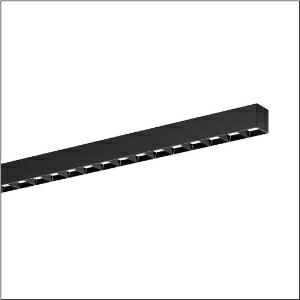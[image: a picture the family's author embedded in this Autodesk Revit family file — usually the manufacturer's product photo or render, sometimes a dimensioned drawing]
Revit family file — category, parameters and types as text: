
# Revit family: silica_r__21_51mx21dc3abb_8748
name_source: partatom
category: Lighting Fixtures
units: mm (PartAtom-declared; Revit-internal decimal feet)

## family parameters
Cut with Voids When Loaded = No
Host = Face
Light Source = No
Part Type = Normal
Room Calculation Point = No
Round Connector Dimension = Use Diameter
Shared = No

## types (1)
- --- (1 x LED, 10800 lm, 69.3 W, 3000K)
    Apparent Load = 69 VA
    CIE Flux Codes = 87 99 100 100 100
    Color Rendering = 80
    Color Temperature = 3000K
    Default Elevation = 1800 mm
    Description = Silica® 21, office luminaire, primary light control with darklight reflector, of PMMA, black, CAT 2 (L<= 3000cd/m²), light emission: direct distribution, primary light characteristic: symmetric, installation type: surface-mounted, LED, rated luminous flux: 10.800lm, luminous efficacy: 156lm/W, light colour: 830, colour temperature: 3000K, with terminal, 3+2-pole, max. 2.5mm², mains connection: 220..240V, AC, 50/60Hz, luminaire housing, of aluminium, jet black (RAL 9005), length: 3.004mm, width: 53mm, height: 53mm, protection rating (complete): IP20, insulation class (complete): insulation class I (protective earthing), certification: CE, permissible operating ambient temperature: 0..+35°C, standard: EN 50419, packaging unit: 1 piece
    Height = 0 mm  [stored 0 ft]
    Lamp = 1 x LED
    Lamp Light Flux = 10800 lm
    Lamp Power = 69.3 W
    Lamp count = 1
    Length = 3004 mm
    Luminous efficacy = 156 lm/W
    Manufacturer = Siteco
    ModVariant = No
    Model = 51MX21DC3ABB
    Mounting Place = Ceiling
    Mounting Type = Recessed
    Number of Poles = 1
    OnlyDefault = Yes
    Power Factor = 1
    Product Name = Silica® 21
    Product group = office luminaire | ceiling recessed
    ProductGroupID = 401
    Protection Class = Protection class I
    Protection Degree = IP 20
    RLX_Detail_Level = 1
    RLX_Emergency_Light_Flux = 0 lm
    RLX_Emergency_Type = 0
    RLX_Emergency_Type_DB = No
    RlxData = <blob elided: 64061 chars, md5=0d5ed433>
    Socket = socket
    Standby Power = 0 W
    System Light Flux = 10800 lm
    System Power = 69 W
    Type Comments = factory setting: luminous flux: 100 % | dim-lin: 254 | 393 mA
    Type Image = l_1313577.jpg
    URL = http://relux.com
    VarID = @adj_072685
    Voltage = 0 V
    Weight = 0.00 kg
    Width = 53 mm

note: [stored X ft] marks values corroborated as IEEE doubles in the binary element streams (Revit-internal decimal feet)

## geometry (parser evidence)
native form markers: Blend x4, Sweep x9
no freeform markers — native parametric forms only
